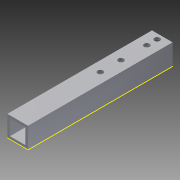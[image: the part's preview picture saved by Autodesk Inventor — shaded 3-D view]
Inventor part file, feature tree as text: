
AUTODESK INVENTOR PART (.ipt)
format: ipt  version: 2013 (Build 170138000, 138)  size: 115,200 bytes
history: native  units: in
note: dims shown in document units (in); Inventor stores cm internally (conversion verified against a paired STEP export)
features: reference x5, sketch x4, extrude x3
ambient origin geometry x8: Origin, YZ Plane, XZ Plane, XY Plane, X Axis, Y Axis, Z Axis, Center Point
bodies: Solid1 (feature_tree)
feature tree (12):
  extrude  "Extrusion1"  Depth=1.0in
  extrude  "Extrusion2"  Depth=7.0in TaperAngle=0.0deg
  extrude  "Extrusion3"  Depth=1.0in TaperAngle=0.0deg
  sketch  "Sketch4"
  sketch  "Sketch1"  dims[d0=1.0in d2=1.0in]
  sketch  "Sketch2"  dims[d3=0.125in d4=7.0in d5=0.0in]
  reference  "Reference1"
  reference  "Reference2"
  sketch  "Sketch3"  dims[d6=1.0in d7=0.0in d8=1.0in d9=0.0in]
  reference  "Reference3"
  reference  "Reference4"
  reference  "Reference5"
